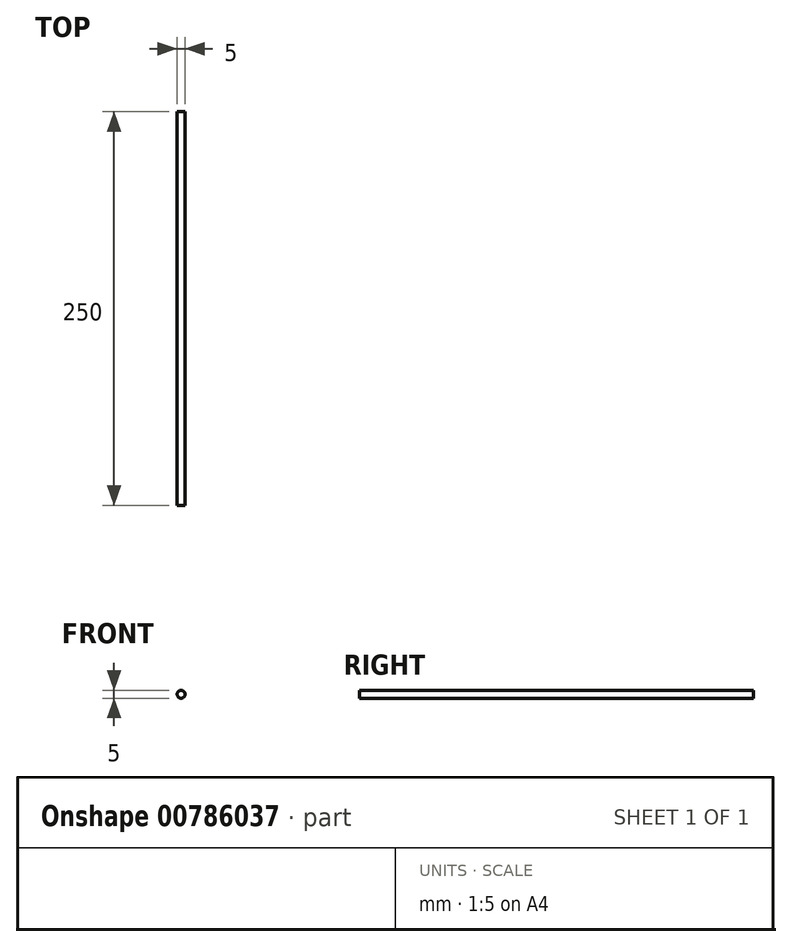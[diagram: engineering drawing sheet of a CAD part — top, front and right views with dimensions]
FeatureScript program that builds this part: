
annotation { "Feature Type Name" : "Feature", "Feature Type Description" : "" }
export const myFeature = defineFeature(function(context is Context, id is Id, definition is map)
    precondition{}
    {
        {
            var Q0;
            Q0=qCreatedBy(makeId("Front.planeOp"),FACE);
            var sketch = newSketch(context, id + "F0", { "sketchPlane" : qUnion([Q0])});
            skCircle(sketch, "E0", {"center": v(0, 0) * mm, "radius": 2.5 * mm});
            skSolve(sketch);
        }
        {
            var Q0;
            Q0=qSketchRegion(id+"F0",true);
            extrude(context, id + "F1", {"entities" : qUnion([Q0]), "depth" : 250 * mm, "offsetDistance" : 25 * mm});
        }
    });
